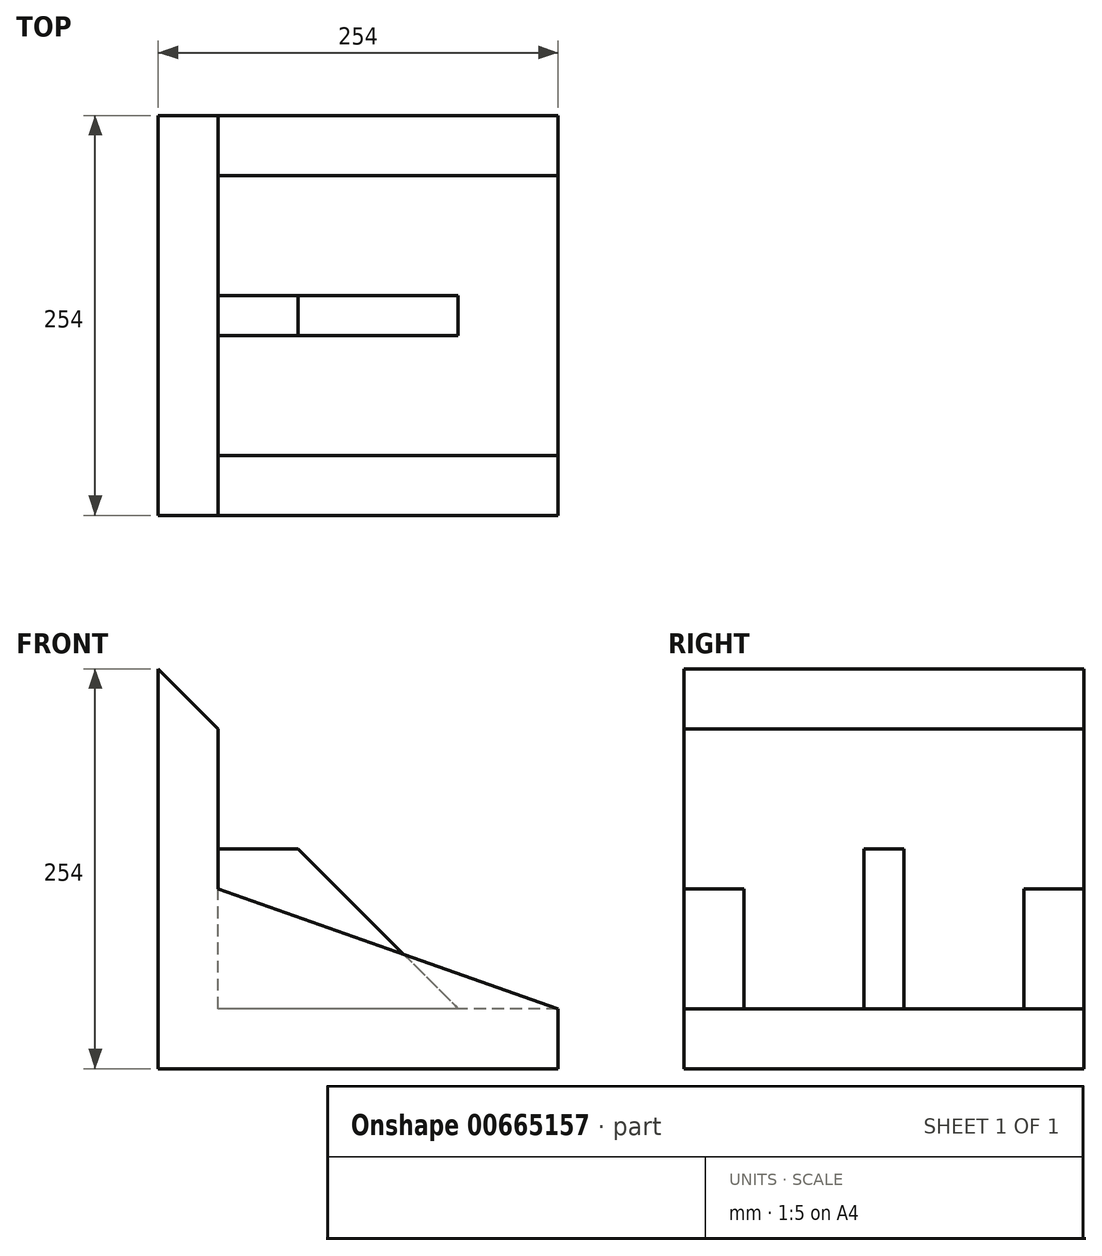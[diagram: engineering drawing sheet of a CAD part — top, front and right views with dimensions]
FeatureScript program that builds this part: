
annotation { "Feature Type Name" : "Feature", "Feature Type Description" : "" }
export const myFeature = defineFeature(function(context is Context, id is Id, definition is map)
    precondition{}
    {
        {
            var Q0;
            Q0=qCreatedBy(makeId("Front.planeOp"),FACE);
            var sketch = newSketch(context, id + "F0", { "sketchPlane" : qUnion([Q0])});
            skLineSegment(sketch, "E0", {"start": v(0, 0) * mm, "end": v(0, 254) * mm});
            skLineSegment(sketch, "E1", {"start": v(0, 0) * mm, "end": v(254, 0) * mm});
            skLineSegment(sketch, "E2", {"start": v(254, 0) * mm, "end": v(254, 38.1) * mm});
            skLineSegment(sketch, "E3", {"start": v(254, 38.1) * mm, "end": v(38.1, 38.1) * mm});
            skLineSegment(sketch, "E4", {"start": v(38.1, 38.1) * mm, "end": v(38.1, 215.9) * mm});
            skLineSegment(sketch, "E5", {"start": v(38.1, 215.9) * mm, "end": v(0, 254) * mm});
            skLineSegment(sketch, "E6", {"start": v(38.1, 139.7) * mm, "end": v(88.9, 139.7) * mm});
            skLineSegment(sketch, "E7", {"start": v(88.9, 139.7) * mm, "end": v(190.5, 38.1) * mm});
            skLineSegment(sketch, "E8", {"start": v(38.1, 139.7) * mm, "end": v(38.1, 38.1) * mm});
            skSolve(sketch);
        }
        {
            var Q0;
            Q0=makeQuery(id+"F0.imprint","IMPRINT",FACE,{"disambiguationData":[TD([[makeQuery(id+"F0.imprint","IMPRINT",EDGE,{"derivedFrom":sQuery(id+"F0.wireOp",EDGE,"E0")}),-1.0]])]});
            extrude(context, id + "F1", {"entities" : qUnion([Q0]), "endBound" : BoundingType.SYMMETRIC, "depth" : 254 * mm, "offsetDistance" : 25.4 * mm});
        }
        {
            var Q0;
            Q0=makeQuery(id+"F0.imprint","IMPRINT",FACE,{"disambiguationData":[TD([[makeQuery(id+"F0.imprint","IMPRINT",EDGE,{"derivedFrom":sQuery(id+"F0.wireOp",EDGE,"E6")}),-1.0]])]});
            extrude(context, id + "F2", {"entities" : qUnion([Q0]), "operationType" : NewBodyOperationType.ADD, "endBound" : BoundingType.SYMMETRIC, "depth" : 25.4 * mm, "offsetDistance" : 25.4 * mm});
        }
        {
            var Q0;
            Q0=makeQuery(id+"F1.opExtrude","CAP_FACE",FACE,{"disambiguationData":[OSD([sQuery(id+"F0.wireOp",EDGE,"E0"),sQuery(id+"F0.wireOp",EDGE,"E1"),sQuery(id+"F0.wireOp",EDGE,"E2"),sQuery(id+"F0.wireOp",EDGE,"E3"),sQuery(id+"F0.wireOp",EDGE,"E4"),sQuery(id+"F0.wireOp",EDGE,"E5"),sQuery(id+"F0.wireOp",EDGE,"E8")])],"isStart":false});
            var sketch = newSketch(context, id + "F3", { "sketchPlane" : qUnion([Q0])});
            skLineSegment(sketch, "E9", {"start": v(38.1, 114.3) * mm, "end": v(254, 38.1) * mm});
            skSolve(sketch);
        }
        {
            var Q0;
            {var subQ0=sQuery(id+"F3.wireOp",EDGE,"E9");Q0=makeQuery(id+"F3.imprint","IMPRINT",FACE,{"disambiguationData":[TD([[makeQuery(id+"F3.imprint","IMPRINT",EDGE,{"derivedFrom":subQ0}),-1.0]])]});}
            extrude(context, id + "F4", {"entities" : qUnion([Q0]), "operationType" : NewBodyOperationType.ADD, "oppositeDirection" : true, "depth" : 38.1 * mm, "offsetDistance" : 25.4 * mm});
        }
        {
            var Q0;
            Q0=makeQuery(id+"F1.opExtrude","CAP_FACE",FACE,{"disambiguationData":[OSD([sQuery(id+"F0.wireOp",EDGE,"E0"),sQuery(id+"F0.wireOp",EDGE,"E1"),sQuery(id+"F0.wireOp",EDGE,"E2"),sQuery(id+"F0.wireOp",EDGE,"E3"),sQuery(id+"F0.wireOp",EDGE,"E4"),sQuery(id+"F0.wireOp",EDGE,"E5"),sQuery(id+"F0.wireOp",EDGE,"E8")])],"isStart":true});
            var sketch = newSketch(context, id + "F5", { "sketchPlane" : qUnion([Q0])});
            skLineSegment(sketch, "E10", {"start": v(-38.1, 114.3) * mm, "end": v(-254, 38.1) * mm});
            skSolve(sketch);
        }
        {
            var Q0;
            {var subQ0=sQuery(id+"F5.wireOp",EDGE,"E10");Q0=makeQuery(id+"F5.imprint","IMPRINT",FACE,{"disambiguationData":[TD([[makeQuery(id+"F5.imprint","IMPRINT",EDGE,{"derivedFrom":subQ0}),1.0]])]});}
            extrude(context, id + "F6", {"entities" : qUnion([Q0]), "operationType" : NewBodyOperationType.ADD, "oppositeDirection" : true, "depth" : 38.1 * mm, "offsetDistance" : 25.4 * mm});
        }
    });
